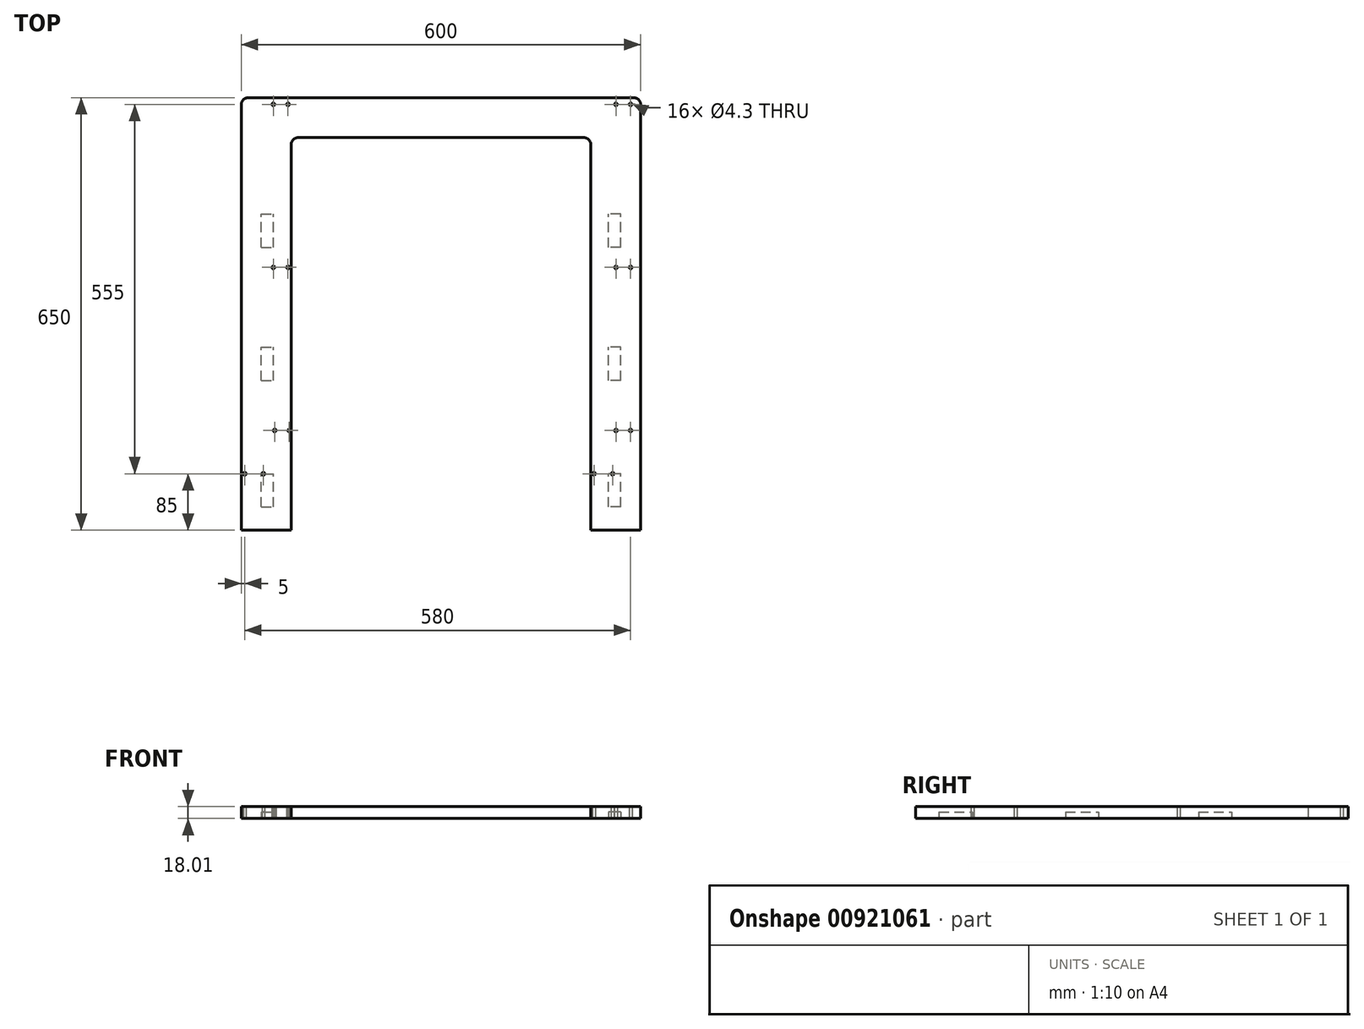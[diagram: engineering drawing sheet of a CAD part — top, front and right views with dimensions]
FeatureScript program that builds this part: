
annotation { "Feature Type Name" : "Feature", "Feature Type Description" : "" }
export const myFeature = defineFeature(function(context is Context, id is Id, definition is map)
    precondition{}
    {
        {
            var Q0;
            Q0=qCreatedBy(makeId("Top.planeOp"),FACE);
            var sketch = newSketch(context, id + "F0", { "sketchPlane" : qUnion([Q0])});
            skLineSegment(sketch, "E0.bottom", {"start": v(0, 0) * mm, "end": v(600, 0) * mm});
            skLineSegment(sketch, "E0.top", {"start": v(0, -650) * mm, "end": v(600, -650) * mm});
            skLineSegment(sketch, "E0.left", {"start": v(0, 0) * mm, "end": v(0, -650) * mm});
            skLineSegment(sketch, "E0.right", {"start": v(600, 0) * mm, "end": v(600, -650) * mm});
            skLineSegment(sketch, "E1.bottom", {"start": v(0, -650) * mm, "end": v(50, -650) * mm});
            skLineSegment(sketch, "E1.top", {"start": v(0, -660) * mm, "end": v(50, -660) * mm});
            skLineSegment(sketch, "E1.left", {"start": v(0, -650) * mm, "end": v(0, -660) * mm});
            skLineSegment(sketch, "E1.right", {"start": v(50, -650) * mm, "end": v(50, -660) * mm});
            skLineSegment(sketch, "E2.bottom", {"start": v(600, -650) * mm, "end": v(550, -650) * mm});
            skLineSegment(sketch, "E2.top", {"start": v(600, -660) * mm, "end": v(550, -660) * mm});
            skLineSegment(sketch, "E2.left", {"start": v(600, -650) * mm, "end": v(600, -660) * mm});
            skLineSegment(sketch, "E2.right", {"start": v(550, -650) * mm, "end": v(550, -660) * mm});
            skLineSegment(sketch, "E3.bottom", {"start": v(75, -650) * mm, "end": v(525, -650) * mm});
            skLineSegment(sketch, "E3.top", {"start": v(75, -60) * mm, "end": v(525, -60) * mm});
            skLineSegment(sketch, "E3.left", {"start": v(75, -650) * mm, "end": v(75, -60) * mm});
            skLineSegment(sketch, "E3.right", {"start": v(525, -650) * mm, "end": v(525, -60) * mm});
            skSolve(sketch);
        }
        {
            var Q0;
            Q0=makeQuery(id+"F0.imprint","IMPRINT",FACE,{"disambiguationData":[TD([[makeQuery(id+"F0.imprint","IMPRINT",EDGE,{"derivedFrom":sQuery(id+"F0.wireOp",EDGE,"E0.bottom")}),-1.0]])]});
            var Q1;
            Q1=makeQuery(id+"F0.imprint","IMPRINT",FACE,{"disambiguationData":[TD([[makeQuery(id+"F0.imprint","IMPRINT",EDGE,{"derivedFrom":sQuery(id+"F0.wireOp",EDGE,"E1.bottom")}),-1.0]])]});
            var Q2;
            Q2=makeQuery(id+"F0.imprint","IMPRINT",FACE,{"disambiguationData":[TD([[makeQuery(id+"F0.imprint","IMPRINT",EDGE,{"derivedFrom":sQuery(id+"F0.wireOp",EDGE,"E2.bottom")}),1.0]])]});
            extrude(context, id + "F1", {"entities" : qUnion([Q0, Q1, Q2]), "depth" : 18 * mm, "offsetDistance" : 25 * mm});
        }
        {
            var Q0;
            Q0=makeQuery(id+"F1.opExtrude","CAP_FACE",FACE,{"disambiguationData":[OSD([sQuery(id+"F0.wireOp",EDGE,"E0.bottom"),sQuery(id+"F0.wireOp",EDGE,"E0.top"),sQuery(id+"F0.wireOp",EDGE,"E0.left"),sQuery(id+"F0.wireOp",EDGE,"E0.right"),sQuery(id+"F0.wireOp",EDGE,"E1.top"),sQuery(id+"F0.wireOp",EDGE,"E1.left"),sQuery(id+"F0.wireOp",EDGE,"E1.right"),sQuery(id+"F0.wireOp",EDGE,"E2.top"),sQuery(id+"F0.wireOp",EDGE,"E2.left"),sQuery(id+"F0.wireOp",EDGE,"E2.right"),sQuery(id+"F0.wireOp",EDGE,"E3.top"),sQuery(id+"F0.wireOp",EDGE,"E3.left"),sQuery(id+"F0.wireOp",EDGE,"E3.right")])],"isStart":true});
            var sketch = newSketch(context, id + "F2", { "sketchPlane" : qUnion([Q0])});
            skLineSegment(sketch, "E4.bottom", {"start": v(30, 615) * mm, "end": v(48, 615) * mm});
            skLineSegment(sketch, "E4.top", {"start": v(30, 565) * mm, "end": v(48, 565) * mm});
            skLineSegment(sketch, "E4.left", {"start": v(30, 615) * mm, "end": v(30, 565) * mm});
            skLineSegment(sketch, "E4.right", {"start": v(48, 615) * mm, "end": v(48, 565) * mm});
            skLineSegment(sketch, "E5.bottom", {"start": v(30, 425) * mm, "end": v(48, 425) * mm});
            skLineSegment(sketch, "E5.top", {"start": v(30, 375) * mm, "end": v(48, 375) * mm});
            skLineSegment(sketch, "E5.left", {"start": v(30, 425) * mm, "end": v(30, 375) * mm});
            skLineSegment(sketch, "E5.right", {"start": v(48, 425) * mm, "end": v(48, 375) * mm});
            skLineSegment(sketch, "E6.bottom", {"start": v(30, 225) * mm, "end": v(48, 225) * mm});
            skLineSegment(sketch, "E6.top", {"start": v(30, 175) * mm, "end": v(48, 175) * mm});
            skLineSegment(sketch, "E6.left", {"start": v(30, 225) * mm, "end": v(30, 175) * mm});
            skLineSegment(sketch, "E6.right", {"start": v(48, 225) * mm, "end": v(48, 175) * mm});
            skLineSegment(sketch, "E7", {"start": v(300, 60) * mm, "end": v(300, 580.5) * mm, "construction": true});
            skLineSegment(sketch, "E8.MirrorCS", {"start": v(552, 425) * mm, "end": v(552, 375) * mm});
            skLineSegment(sketch, "E9.MirrorCS", {"start": v(570, 425) * mm, "end": v(570, 375) * mm});
            skLineSegment(sketch, "E10.MirrorCS", {"start": v(570, 225) * mm, "end": v(570, 175) * mm});
            skLineSegment(sketch, "E11.MirrorCS", {"start": v(570, 615) * mm, "end": v(570, 565) * mm});
            skLineSegment(sketch, "E12.MirrorCS", {"start": v(570, 175) * mm, "end": v(552, 175) * mm});
            skLineSegment(sketch, "E13.MirrorCS", {"start": v(570, 425) * mm, "end": v(552, 425) * mm});
            skLineSegment(sketch, "E14.MirrorCS", {"start": v(552, 615) * mm, "end": v(552, 565) * mm});
            skLineSegment(sketch, "E15.MirrorCS", {"start": v(570, 615) * mm, "end": v(552, 615) * mm});
            skLineSegment(sketch, "E16.MirrorCS", {"start": v(570, 225) * mm, "end": v(552, 225) * mm});
            skLineSegment(sketch, "E17.MirrorCS", {"start": v(552, 225) * mm, "end": v(552, 175) * mm});
            skLineSegment(sketch, "E18.MirrorCS", {"start": v(570, 565) * mm, "end": v(552, 565) * mm});
            skLineSegment(sketch, "E19.MirrorCS", {"start": v(570, 375) * mm, "end": v(552, 375) * mm});
            skSolve(sketch);
        }
        {
            var Q0;
            Q0=makeQuery(id+"F2.imprint","IMPRINT",FACE,{"disambiguationData":[TD([[makeQuery(id+"F2.imprint","IMPRINT",EDGE,{"derivedFrom":sQuery(id+"F2.wireOp",EDGE,"E4.bottom")}),-1.0]])]});
            var Q1;
            Q1=makeQuery(id+"F2.imprint","IMPRINT",FACE,{"disambiguationData":[TD([[makeQuery(id+"F2.imprint","IMPRINT",EDGE,{"derivedFrom":sQuery(id+"F2.wireOp",EDGE,"E5.bottom")}),-1.0]])]});
            var Q2;
            Q2=makeQuery(id+"F2.imprint","IMPRINT",FACE,{"disambiguationData":[TD([[makeQuery(id+"F2.imprint","IMPRINT",EDGE,{"derivedFrom":sQuery(id+"F2.wireOp",EDGE,"E6.bottom")}),-1.0]])]});
            var Q3;
            Q3=makeQuery(id+"F2.imprint","IMPRINT",FACE,{"disambiguationData":[TD([[makeQuery(id+"F2.imprint","IMPRINT",EDGE,{"derivedFrom":sQuery(id+"F2.wireOp",EDGE,"E10.MirrorCS")}),-1.0]])]});
            var Q4;
            Q4=makeQuery(id+"F2.imprint","IMPRINT",FACE,{"disambiguationData":[TD([[makeQuery(id+"F2.imprint","IMPRINT",EDGE,{"derivedFrom":sQuery(id+"F2.wireOp",EDGE,"E13.MirrorCS")}),1.0]])]});
            var Q5;
            Q5=makeQuery(id+"F2.imprint","IMPRINT",FACE,{"disambiguationData":[TD([[makeQuery(id+"F2.imprint","IMPRINT",EDGE,{"derivedFrom":sQuery(id+"F2.wireOp",EDGE,"E14.MirrorCS")}),1.0]])]});
            extrude(context, id + "F3", {"entities" : qUnion([Q0, Q1, Q2, Q3, Q4, Q5]), "operationType" : NewBodyOperationType.REMOVE, "oppositeDirection" : true, "depth" : 10 * mm, "offsetDistance" : 25 * mm});
        }
        {
            var Q0;
            Q0=makeQuery(id+"F1.opExtrude","CAP_FACE",FACE,{"disambiguationData":[OSD([sQuery(id+"F0.wireOp",EDGE,"E0.bottom"),sQuery(id+"F0.wireOp",EDGE,"E0.top"),sQuery(id+"F0.wireOp",EDGE,"E0.left"),sQuery(id+"F0.wireOp",EDGE,"E0.right"),sQuery(id+"F0.wireOp",EDGE,"E1.top"),sQuery(id+"F0.wireOp",EDGE,"E1.left"),sQuery(id+"F0.wireOp",EDGE,"E1.right"),sQuery(id+"F0.wireOp",EDGE,"E2.top"),sQuery(id+"F0.wireOp",EDGE,"E2.left"),sQuery(id+"F0.wireOp",EDGE,"E2.right"),sQuery(id+"F0.wireOp",EDGE,"E3.top"),sQuery(id+"F0.wireOp",EDGE,"E3.left"),sQuery(id+"F0.wireOp",EDGE,"E3.right")])],"isStart":false});
            var sketch = newSketch(context, id + "F4", { "sketchPlane" : qUnion([Q0])});
            skLineSegment(sketch, "E20.bottom", {"start": v(563, -10) * mm, "end": v(585, -10) * mm});
            skLineSegment(sketch, "E20.top", {"start": v(563, -500) * mm, "end": v(585, -500) * mm});
            skLineSegment(sketch, "E20.left", {"start": v(563, -10) * mm, "end": v(563, -500) * mm});
            skLineSegment(sketch, "E20.right", {"start": v(585, -10) * mm, "end": v(585, -500) * mm});
            skPoint(sketch, "E21", {"position": v(563, -255) * mm});
            skPoint(sketch, "E22", {"position": v(585, -255) * mm});
            skPoint(sketch, "E23", {"position": v(563, -10) * mm});
            skPoint(sketch, "E24", {"position": v(585, -10) * mm});
            skPoint(sketch, "E25", {"position": v(563, -500) * mm});
            skPoint(sketch, "E26", {"position": v(585, -500) * mm});
            skPoint(sketch, "E27.MirrorP", {"position": v(70, -10) * mm});
            skPoint(sketch, "E28.MirrorP", {"position": v(48, -10) * mm});
            skPoint(sketch, "E29.MirrorP", {"position": v(70, -255) * mm});
            skPoint(sketch, "E30.MirrorP", {"position": v(48, -255) * mm});
            skPoint(sketch, "E31.MirrorP", {"position": v(72, -500) * mm});
            skPoint(sketch, "E32.MirrorP", {"position": v(50, -500) * mm});
            skLineSegment(sketch, "E33", {"start": v(563, -500) * mm, "end": v(563, -565) * mm, "construction": true});
            skLineSegment(sketch, "E34", {"start": v(563, -565) * mm, "end": v(525, -565) * mm, "construction": true});
            skPoint(sketch, "E35", {"position": v(558, -565) * mm});
            skPoint(sketch, "E36", {"position": v(530, -565) * mm});
            skPoint(sketch, "E37.MirrorP", {"position": v(5, -565) * mm});
            skPoint(sketch, "E38.MirrorP", {"position": v(33, -565) * mm});
            skSolve(sketch);
        }
        {
            var Q0;
            Q0=sQuery(id+"F4.wireOp",VERTEX,"E20.bottom.start");
            var Q1;
            Q1=sQuery(id+"F4.wireOp",VERTEX,"E20.bottom.end");
            var Q2;
            Q2=sQuery(id+"F4.wireOp",VERTEX,"E21");
            var Q3;
            Q3=sQuery(id+"F4.wireOp",VERTEX,"E20.top.start");
            var Q4;
            Q4=sQuery(id+"F4.wireOp",VERTEX,"E20.top.end");
            var Q5;
            Q5=sQuery(id+"F4.wireOp",VERTEX,"E22");
            var Q6;
            Q6=sQuery(id+"F4.wireOp",VERTEX,"E28.MirrorP");
            var Q7;
            Q7=sQuery(id+"F4.wireOp",VERTEX,"E27.MirrorP");
            var Q8;
            Q8=sQuery(id+"F4.wireOp",VERTEX,"E30.MirrorP");
            var Q9;
            Q9=sQuery(id+"F4.wireOp",VERTEX,"E29.MirrorP");
            var Q10;
            Q10=sQuery(id+"F4.wireOp",VERTEX,"E32.MirrorP");
            var Q11;
            Q11=sQuery(id+"F4.wireOp",VERTEX,"E31.MirrorP");
            var Q12;
            Q12=sQuery(id+"F4.wireOp",VERTEX,"E36");
            var Q13;
            Q13=sQuery(id+"F4.wireOp",VERTEX,"E35");
            var Q14;
            Q14=sQuery(id+"F4.wireOp",VERTEX,"7015efea-0abc-41e5-8ae3-410e3846c2380.MirrorP");
            var Q15;
            Q15=sQuery(id+"F4.wireOp",VERTEX,"7015efea-0abc-41e5-8ae3-410e3846c2381.MirrorP");
            var Q16;
            Q16=sQuery(id+"F4.wireOp",VERTEX,"E37.MirrorP");
            var Q17;
            Q17=sQuery(id+"F4.wireOp",VERTEX,"E38.MirrorP");
            var Q18;
            Q18=makeQuery(id+"F1.opExtrude","SWEPT_BODY",BODY,{"disambiguationData":[OSD([sQuery(id+"F0.wireOp",EDGE,"E0.bottom"),sQuery(id+"F0.wireOp",EDGE,"E0.top"),sQuery(id+"F0.wireOp",EDGE,"E0.left"),sQuery(id+"F0.wireOp",EDGE,"E0.right"),sQuery(id+"F0.wireOp",EDGE,"E1.top"),sQuery(id+"F0.wireOp",EDGE,"E1.left"),sQuery(id+"F0.wireOp",EDGE,"E1.right"),sQuery(id+"F0.wireOp",EDGE,"E2.top"),sQuery(id+"F0.wireOp",EDGE,"E2.left"),sQuery(id+"F0.wireOp",EDGE,"E2.right"),sQuery(id+"F0.wireOp",EDGE,"E3.top"),sQuery(id+"F0.wireOp",EDGE,"E3.left"),sQuery(id+"F0.wireOp",EDGE,"E3.right")])]});
            hole(context, id + "F5", {"style" : HoleStyle.SIMPLE, "endStyle" : HoleEndStyle.THROUGH, "standardTappedOrClearance" : lookupTablePath({ "fit" : "Close", "standard" : "ISO", "size" : "M4", "type" : "Clearance" }), "standardBlindInLast" : lookupTablePath({ "fit" : "Close", "standard" : "ISO", "size" : "M4", "type" : "Clearance" }), "holeDiameter" : 4.3 * mm, "majorDiameter" : 5 * mm, "tappedDepth" : 12.9 * mm, "tapClearance" : 3, "locations" : qUnion([Q0, Q1, Q2, Q3, Q4, Q5, Q6, Q7, Q8, Q9, Q10, Q11, Q12, Q13, Q14, Q15, Q16, Q17]), "scope" : qUnion([Q18])});
        }
        {
            var Q0;
            Q0=makeQuery(id+"F1.opExtrude","SWEPT_EDGE",EDGE,{"disambiguationData":[OSD([sQuery(id+"F0.wireOp",EDGE,"E3.top"),sQuery(id+"F0.wireOp",EDGE,"E3.left")])]});
            var Q1;
            Q1=makeQuery(id+"F1.opExtrude","SWEPT_EDGE",EDGE,{"disambiguationData":[OSD([sQuery(id+"F0.wireOp",EDGE,"E3.top"),sQuery(id+"F0.wireOp",EDGE,"E3.right")])]});
            fillet(context, id + "F6", {"entities" : qUnion([Q0, Q1]), "radius" : 10 * mm, "tangentPropagation" : true, "allowEdgeOverflow" : false});
        }
        {
            var Q0;
            Q0=makeQuery(id+"F1.opExtrude","SWEPT_EDGE",EDGE,{"disambiguationData":[OSD([sQuery(id+"F0.wireOp",EDGE,"E0.bottom"),sQuery(id+"F0.wireOp",EDGE,"E0.right")])]});
            var Q1;
            Q1=makeQuery(id+"F1.opExtrude","SWEPT_EDGE",EDGE,{"disambiguationData":[OSD([sQuery(id+"F0.wireOp",EDGE,"E0.bottom"),sQuery(id+"F0.wireOp",EDGE,"E0.left")])]});
            fillet(context, id + "F7", {"entities" : qUnion([Q0, Q1]), "radius" : 10 * mm, "tangentPropagation" : true, "allowEdgeOverflow" : false});
        }
    });
